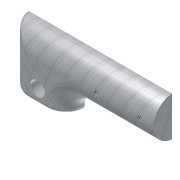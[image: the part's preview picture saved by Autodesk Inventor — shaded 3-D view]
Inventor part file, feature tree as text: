
AUTODESK INVENTOR PART (.ipt)
format: ipt  version: unknown  size: 239,104 bytes
history: native  units: in
note: dims shown in document units (in); Inventor stores cm internally (conversion verified against a paired STEP export)
features: extrude x2, fillet x2, hole x2, sketch x2, pattern_linear x1
ambient origin geometry x8: Origin, YZ Plane, XZ Plane, XY Plane, X Axis, Y Axis, Z Axis, Center Point
feature tree (9):
  extrude  "Extrusion1"  Depth=1.375in
  fillet  "Fillet1"  Radius=2.0in
  fillet  "Fillet2"  Radius=5.0in
  extrude  "Extrusion2"  Depth=0.4375in
  hole  "Hole1"  [1 undecoded]
  pattern_linear  "Rectangular Pattern1"  Spacing1=0.125in  [1 undecoded]
  hole  "Hole2"  [1 undecoded]
  sketch  "Sketch1"  dims[d0=2.0in d1=1.375in d2=2.0in d3=5.0in]
  sketch  "Sketch2"  dims[d6=0.75in d7=0.0in d8=0.4375in d9=0.6875in d10=0.125in d11=0.125in d12=8.0in d13=42.0in d14=0.0in d15=0.6875in d16=0.5in d17=0.196in d18=0.5in d19=0.375in d20=0.25in d21=0.5635in d22=0.75in d23=0.8108in d24=0.7874in d26=1.5in d27=4.0in d28=0.456in d29=0.5in d30=0.5in d31=0.375in d32=0.25in d33=0.5635in d34=0.75in d35=0.8108in]
note: 3 required parameter values undecoded (feature->parameter linkage not recoverable at this tier; creation-order binding heuristic only, values carry confidence <= 0.55)
